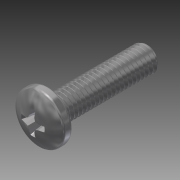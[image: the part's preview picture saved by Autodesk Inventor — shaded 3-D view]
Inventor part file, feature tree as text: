
AUTODESK INVENTOR PART (.ipt)
format: ipt  version: 2014 SP1 (Build 180222100, 222)  size: 738,816 bytes
history: native  units: in
note: dims shown in document units (in); Inventor stores cm internally (conversion verified against a paired STEP export)
features: fillet x1, other x1, imported_body x1
ambient origin geometry x8: Origin, YZ Plane, XZ Plane, XY Plane, X Axis, Y Axis, Z Axis, Center Point
bodies: Body1 (feature_tree)
feature tree (3):
  fillet  "Fillet1"  [1 undecoded]
  other  "91735A8311"
  imported_body  "Base1"
note: 1 required parameter value undecoded (feature->parameter linkage not recoverable at this tier; creation-order binding heuristic only, values carry confidence <= 0.55)
